# Revit family: CS2 (2RED+2RJ45)
name_source: partatom
category: Aparatos eléctricos
revit_build: Autodesk Revit 2017 (Build: 20171027_0315(x64)
units: mm (PartAtom-declared; Revit-internal decimal feet)

## family parameters
Anfitrión = Cara
Compartido = No
Corte con vacíos al cargar = No
Cota de conector redondo = Diámetro de uso
Mantener orientación de anotación = No
Número OmniClass = 23.80.50.11.11
Punto de cálculo de habitación = No
Tipo de pieza = Normal
Título OmniClass = Receptacle Terminal Units

## types (1)
- Módulo /4 - Blanco
    Acabado = Blanco nieve RAL9010
    CS2 (AltoxLargoxAncho) = 150 x 147,5 x 69 mm
    Capacidad = Ilimitada
    Carga eléctrica = Potencia
    Compatibilidad = Gama Plus
    Composición = Cubeta, Marco, Bastidor, Tornillería montaje en superficie (2ud), Laterales (2ud), Tapa para canaleta
    Conexiones = 2 tomas de corriente estándar + 2 conexiones de red RJ45
    Código de montaje = D5020100
    Descripción = Caja de conexiones tipo CS2 PLUS
    Elevación por defecto = 1200 mm
    Fabricante = MMCONECTA
    Factor de potencia = 1
    Instalación = Superficie
    Materia prima = Policarbonato libre de halógenos
    Modelo = CS2
    Normativas = UNE 20451 / Marcado CE
    Polos = 1
    Potencia aparente = 3500 W
    URL = http://www.mmconecta.com
    Voltaje = 230 V
    Ø tubo = 15 mm  [stored 0.0492126 ft]

note: [stored X ft] marks values corroborated as IEEE doubles in the binary element streams (Revit-internal decimal feet)

## geometry (parser evidence)
native form markers: Blend x4
no freeform markers — native parametric forms only
